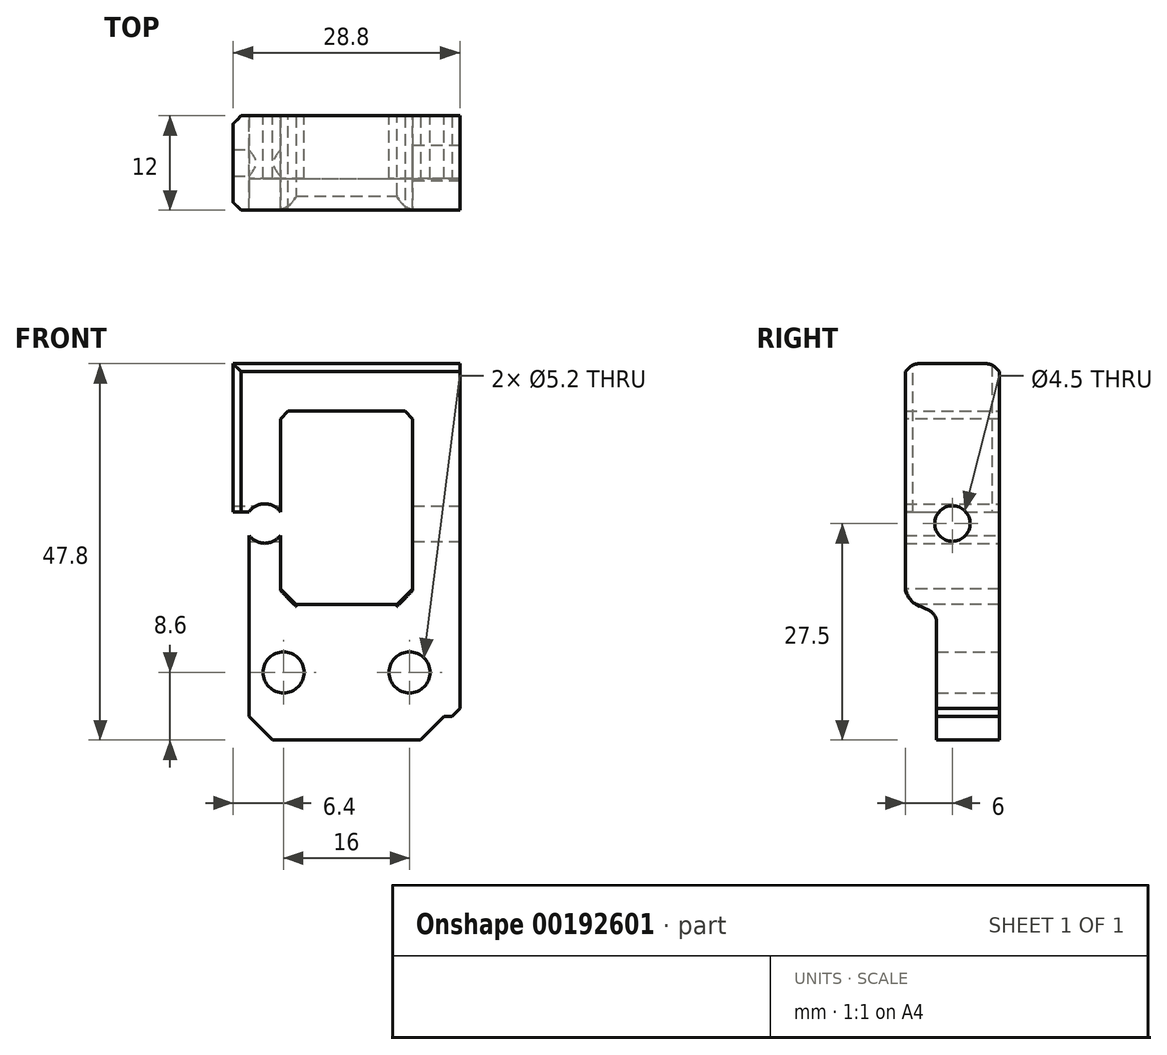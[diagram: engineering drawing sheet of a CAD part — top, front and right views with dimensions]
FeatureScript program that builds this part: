
annotation { "Feature Type Name" : "Feature", "Feature Type Description" : "" }
export const myFeature = defineFeature(function(context is Context, id is Id, definition is map)
    precondition{}
    {
        {
            var Q0;
            Q0=qCreatedBy(makeId("Front.planeOp"),FACE);
            var sketch = newSketch(context, id + "F0", { "sketchPlane" : qUnion([Q0])});
            skLineSegment(sketch, "E0", {"start": v(0, 0) * mm, "end": v(24.8, 0) * mm});
            skLineSegment(sketch, "E1", {"start": v(24.8, 0) * mm, "end": v(24.8, 41.8) * mm});
            skLineSegment(sketch, "E2", {"start": v(24.8, 41.8) * mm, "end": v(20.8, 41.8) * mm});
            skLineSegment(sketch, "E3", {"start": v(20.8, 41.8) * mm, "end": v(20.8, 17.2) * mm});
            skLineSegment(sketch, "E4", {"start": v(20.8, 17.2) * mm, "end": v(4, 17.2) * mm});
            skLineSegment(sketch, "E5", {"start": v(4, 17.2) * mm, "end": v(4, 27.5) * mm});
            skLineSegment(sketch, "E6", {"start": v(4, 27.5) * mm, "end": v(0, 27.5) * mm});
            skLineSegment(sketch, "E7", {"start": v(0, 27.5) * mm, "end": v(0, 0) * mm});
            skLineSegment(sketch, "E8", {"start": v(12.4, 17.2) * mm, "end": v(12.4, 0) * mm});
            skCircle(sketch, "E9", {"center": v(4.4, 8.6) * mm, "radius": 2.6 * mm});
            skPoint(sketch, "E9.centerSnap0", {"position": v(12.4, 8.6) * mm});
            skCircle(sketch, "E10", {"center": v(20.4, 8.6) * mm, "radius": 2.6 * mm});
            skCircle(sketch, "E11", {"center": v(2, 27.5) * mm, "radius": 2.5 * mm});
            skLineSegment(sketch, "E12.bottom", {"start": v(0, 27.5) * mm, "end": v(4, 27.5) * mm});
            skLineSegment(sketch, "E12.top", {"start": v(0, 41.8) * mm, "end": v(4, 41.8) * mm});
            skLineSegment(sketch, "E12.left", {"start": v(0, 27.5) * mm, "end": v(0, 41.8) * mm});
            skLineSegment(sketch, "E12.right", {"start": v(4, 27.5) * mm, "end": v(4, 41.8) * mm});
            skLineSegment(sketch, "E13", {"start": v(0, 41.8) * mm, "end": v(0, 47.8) * mm});
            skLineSegment(sketch, "E14", {"start": v(0, 47.8) * mm, "end": v(24.8, 47.8) * mm});
            skLineSegment(sketch, "E15", {"start": v(24.8, 47.8) * mm, "end": v(24.8, 41.8) * mm});
            skLineSegment(sketch, "E16", {"start": v(4, 41.8) * mm, "end": v(20.8, 41.8) * mm});
            skLineSegment(sketch, "E17", {"start": v(20.4, 8.6) * mm, "end": v(20.4, 11.2) * mm});
            skSolve(sketch);
        }
        {
            var Q0;
            {var subQ5=sQuery(id+"F0.wireOp",EDGE,"E12.top");Q0=makeQuery(id+"F0.imprint","IMPRINT",FACE,{"disambiguationData":[TD([[makeQuery(id+"F0.imprint","IMPRINT",EDGE,{"derivedFrom":subQ5}),-1.0]])]});}
            var Q1;
            {var subQ5=sQuery(id+"F0.wireOp",EDGE,"E12.bottom");Q1=makeQuery(id+"F0.imprint","IMPRINT",FACE,{"disambiguationData":[TD([[makeQuery(id+"F0.imprint","IMPRINT",EDGE,{"derivedFrom":subQ5}),1.0]])]});}
            var Q2;
            {var subQ0=sQuery(id+"F0.wireOp",EDGE,"E12.bottom");Q2=makeQuery(id+"F0.imprint","IMPRINT",FACE,{"disambiguationData":[TD([[makeQuery(id+"F0.imprint","IMPRINT",EDGE,{"derivedFrom":subQ0}),-1.0]])]});}
            var Q3;
            {var subQ9=sQuery(id+"F0.wireOp",EDGE,"E8");Q3=makeQuery(id+"F0.imprint","IMPRINT",FACE,{"disambiguationData":[TD([[makeQuery(id+"F0.imprint","IMPRINT",EDGE,{"derivedFrom":subQ9}),-1.0]])]});}
            var Q4;
            {var subQ1=sQuery(id+"F0.wireOp",EDGE,"E1");Q4=makeQuery(id+"F0.imprint","IMPRINT",FACE,{"disambiguationData":[TD([[makeQuery(id+"F0.imprint","IMPRINT",EDGE,{"derivedFrom":subQ1}),1.0]])]});}
            var Q5;
            Q5=makeQuery(id+"F0.imprint","IMPRINT",FACE,{"disambiguationData":[TD([[makeQuery(id+"F0.imprint","IMPRINT",EDGE,{"derivedFrom":sQuery(id+"F0.wireOp",EDGE,"E2")}),-1.0]])]});
            extrude(context, id + "F1", {"entities" : qUnion([Q0, Q1, Q2, Q3, Q4, Q5]), "depth" : 12 * mm});
        }
        {
            var Q0;
            Q0=makeQuery(id+"F1.opExtrude","SWEPT_FACE",FACE,{"disambiguationData":[OSD([sQuery(id+"F0.wireOp",EDGE,"E1")])]});
            var sketch = newSketch(context, id + "F2", { "sketchPlane" : qUnion([Q0])});
            skCircle(sketch, "E18", {"center": v(-6, 27.5) * mm, "radius": 2.25 * mm});
            skPoint(sketch, "E18.centerSnap0", {"position": v(-6, 0) * mm});
            skLineSegment(sketch, "E19", {"start": v(-8, 0) * mm, "end": v(-8, 16) * mm});
            skLineSegment(sketch, "E20", {"start": v(-8, 16) * mm, "end": v(-12, 17.87) * mm});
            skSolve(sketch);
        }
        {
            var Q0;
            {var subQ0=sQuery(id+"F2.wireOp",EDGE,"E19");Q0=makeQuery(id+"F2.imprint","IMPRINT",FACE,{"disambiguationData":[TD([[makeQuery(id+"F2.imprint","IMPRINT",EDGE,{"derivedFrom":subQ0}),1.0]])]});}
            var Q1;
            Q1=makeQuery(id+"F2.imprint","IMPRINT",FACE,{"disambiguationData":[TD([[makeQuery(id+"F2.imprint","IMPRINT",EDGE,{"derivedFrom":sQuery(id+"F2.wireOp",EDGE,"E18")}),1.0]])]});
            extrude(context, id + "F3", {"entities" : qUnion([Q0, Q1]), "operationType" : NewBodyOperationType.REMOVE, "oppositeDirection" : true, "depth" : 28.8 * mm});
        }
        {
            var Q0;
            Q0=makeQuery(id+"F1.opExtrude","SWEPT_EDGE",EDGE,{"disambiguationData":[OSD([sQuery(id+"F0.wireOp",EDGE,"E4"),sQuery(id+"F0.wireOp",EDGE,"E5")])]});
            var Q1;
            Q1=makeQuery(id+"F1.opExtrude","SWEPT_EDGE",EDGE,{"disambiguationData":[OSD([sQuery(id+"F0.wireOp",EDGE,"E3"),sQuery(id+"F0.wireOp",EDGE,"E4")])]});
            chamfer(context, id + "F4", {"entities" : qUnion([Q0, Q1]), "width" : 2 * mm, "tangentPropagation" : true});
        }
        {
            var Q0;
            Q0=makeQuery(id+"F1.opExtrude","CAP_EDGE",EDGE,{"disambiguationData":[OSD([sQuery(id+"F0.wireOp",EDGE,"E14")])],"isStart":false});
            var Q1;
            Q1=makeQuery(id+"F1.opExtrude","SWEPT_EDGE",EDGE,{"disambiguationData":[OSD([sQuery(id+"F0.wireOp",EDGE,"E12.top"),sQuery(id+"F0.wireOp",EDGE,"E12.right"),sQuery(id+"F0.wireOp",EDGE,"E16")])]});
            var Q2;
            Q2=makeQuery(id+"F1.opExtrude","SWEPT_EDGE",EDGE,{"disambiguationData":[OSD([sQuery(id+"F0.wireOp",EDGE,"E2"),sQuery(id+"F0.wireOp",EDGE,"E3"),sQuery(id+"F0.wireOp",EDGE,"E16")])]});
            var Q3;
            Q3=makeQuery(id+"F1.opExtrude","CAP_EDGE",EDGE,{"disambiguationData":[OSD([sQuery(id+"F0.wireOp",EDGE,"E14")])],"isStart":true});
            chamfer(context, id + "F5", {"entities" : qUnion([Q0, Q1, Q2, Q3]), "width" : 1 * mm, "tangentPropagation" : true});
        }
        {
            var Q0;
            {var subQ0=sQuery(id+"F0.wireOp",EDGE,"E12.right");var subQ3=sQuery(id+"F0.wireOp",EDGE,"E5");var subQ4=sQuery(id+"F0.wireOp",EDGE,"E1");var subQ5=sQuery(id+"F2.wireOp",EDGE,"E20");Q0=makeQuery(id+"F3.boolean.opBoolean","COPY",EDGE,{"disambiguationData":[TD([makeQuery(id+"F1.opExtrude","SWEPT_FACE",FACE,{"disambiguationData":[OSD([subQ3,subQ0])]})])],"derivedFrom":makeQuery(id+"F3.opExtrude","SWEPT_EDGE",EDGE,{"disambiguationData":[OSD([subQ4,subQ5])]})});}
            var Q1;
            {var subQ1=sQuery(id+"F0.wireOp",EDGE,"E1");var subQ2=sQuery(id+"F2.wireOp",EDGE,"E20");Q1=makeQuery(id+"F3.boolean.opBoolean","COPY",EDGE,{"disambiguationData":[TD([makeQuery(id+"F1.opExtrude","SWEPT_FACE",FACE,{"disambiguationData":[OSD([subQ1])]})])],"derivedFrom":makeQuery(id+"F3.opExtrude","SWEPT_EDGE",EDGE,{"disambiguationData":[OSD([subQ1,subQ2])]})});}
            fillet(context, id + "F6", {"entities" : qUnion([Q0, Q1]), "radius" : 2.7 * mm, "tangentPropagation" : true, "allowEdgeOverflow" : false});
        }
        {
            var Q0;
            Q0=makeQuery(id+"F1.opExtrude","SWEPT_EDGE",EDGE,{"disambiguationData":[OSD([sQuery(id+"F0.wireOp",EDGE,"E0"),sQuery(id+"F0.wireOp",EDGE,"E1")])]});
            var Q1;
            Q1=makeQuery(id+"F1.opExtrude","SWEPT_EDGE",EDGE,{"disambiguationData":[OSD([sQuery(id+"F0.wireOp",EDGE,"E0"),sQuery(id+"F0.wireOp",EDGE,"E7")])]});
            chamfer(context, id + "F7", {"entities" : qUnion([Q0, Q1]), "width" : 3 * mm, "tangentPropagation" : true});
        }
        {
            var Q0;
            Q0=makeQuery(id+"F1.opExtrude","SWEPT_FACE",FACE,{"disambiguationData":[OSD([sQuery(id+"F0.wireOp",EDGE,"E7"),sQuery(id+"F0.wireOp",EDGE,"E12.left"),sQuery(id+"F0.wireOp",EDGE,"E13")])]});
            extrude(context, id + "F8", {"entities" : qUnion([Q0]), "operationType" : NewBodyOperationType.ADD, "depth" : 2 * mm});
        }
        {
            var Q0;
            Q0=makeQuery(id+"F1.opExtrude","SWEPT_FACE",FACE,{"disambiguationData":[OSD([sQuery(id+"F0.wireOp",EDGE,"E1"),sQuery(id+"F0.wireOp",EDGE,"E15")])]});
            extrude(context, id + "F9", {"entities" : qUnion([Q0]), "operationType" : NewBodyOperationType.ADD, "depth" : 2 * mm});
        }
        {
            var Q0;
            Q0=makeQuery(id+"F8.opExtrude","CAP_EDGE",EDGE,{"disambiguationData":[OSD([sQuery(id+"F0.wireOp",EDGE,"E0"),sQuery(id+"F0.wireOp",EDGE,"E7"),sQuery(id+"F0.wireOp",EDGE,"E12.left"),sQuery(id+"F0.wireOp",EDGE,"E13")])],"isStart":false});
            var Q1;
            Q1=makeQuery(id+"F9.opExtrude","CAP_EDGE",EDGE,{"disambiguationData":[OSD([sQuery(id+"F0.wireOp",EDGE,"E0"),sQuery(id+"F0.wireOp",EDGE,"E1"),sQuery(id+"F0.wireOp",EDGE,"E15")])],"isStart":false});
            chamfer(context, id + "F10", {"entities" : qUnion([Q0, Q1]), "width" : 1 * mm, "tangentPropagation" : true});
        }
        {
            var Q0;
            {var subQ0=sQuery(id+"F2.wireOp",EDGE,"E20");var subQ1=sQuery(id+"F2.wireOp",EDGE,"E19");Q0=makeQuery(id+"F9.boolean.opBoolean","MERGE",EDGE,{"derivedFrom":[makeQuery(id+"F8.boolean.opBoolean","MERGE",EDGE,{"derivedFrom":[makeQuery(id+"F3.boolean.opBoolean","COPY",EDGE,{"derivedFrom":makeQuery(id+"F3.opExtrude","SWEPT_EDGE",EDGE,{"disambiguationData":[OSD([subQ1,subQ0])]})}),makeQuery(id+"F8.opExtrude","SWEPT_EDGE",EDGE,{"disambiguationData":[OSD([sQuery(id+"F0.wireOp",EDGE,"E7"),sQuery(id+"F0.wireOp",EDGE,"E12.left"),sQuery(id+"F0.wireOp",EDGE,"E13"),subQ1,subQ0])]})]}),makeQuery(id+"F9.opExtrude","SWEPT_EDGE",EDGE,{"disambiguationData":[OSD([subQ1,subQ0])]})]});}
            fillet(context, id + "F11", {"entities" : qUnion([Q0]), "radius" : 1.62 * mm, "tangentPropagation" : true, "allowEdgeOverflow" : false});
        }
        {
            var Q0;
            {var subQ0=sQuery(id+"F0.wireOp",EDGE,"E4");var subQ1=sQuery(id+"F0.wireOp",EDGE,"E15");var subQ3=sQuery(id+"F0.wireOp",EDGE,"E12.right");var subQ6=sQuery(id+"F0.wireOp",EDGE,"E5");var subQ7=sQuery(id+"F0.wireOp",EDGE,"E1");var subQ8=sQuery(id+"F2.wireOp",EDGE,"E20");Q0=makeQuery(id+"F6.opFillet","BLEND_EDGE",EDGE,{"blendedFrom":[makeQuery(id+"F3.boolean.opBoolean","COPY",EDGE,{"disambiguationData":[TD([makeQuery(id+"F1.opExtrude","SWEPT_FACE",FACE,{"disambiguationData":[OSD([subQ6,subQ3])]})])],"derivedFrom":makeQuery(id+"F3.opExtrude","SWEPT_EDGE",EDGE,{"disambiguationData":[OSD([subQ7,subQ1,subQ8])]})}),makeQuery(id+"F1.opExtrude","SWEPT_FACE",FACE,{"disambiguationData":[OSD([subQ0])]})],"blendedInto":[makeQuery(id+"F1.opExtrude","SWEPT_FACE",FACE,{"disambiguationData":[OSD([subQ0])]})]});}
            var Q1;
            {var subQ0=sQuery(id+"F0.wireOp",EDGE,"E5");var subQ1=sQuery(id+"F0.wireOp",EDGE,"E4");var subQ2=sQuery(id+"F0.wireOp",EDGE,"E15");var subQ4=sQuery(id+"F0.wireOp",EDGE,"E12.right");var subQ7=sQuery(id+"F0.wireOp",EDGE,"E1");var subQ8=sQuery(id+"F2.wireOp",EDGE,"E20");Q1=makeQuery(id+"F6.opFillet","BLEND_EDGE",EDGE,{"blendedFrom":[makeQuery(id+"F3.boolean.opBoolean","COPY",EDGE,{"disambiguationData":[TD([makeQuery(id+"F1.opExtrude","SWEPT_FACE",FACE,{"disambiguationData":[OSD([subQ0,subQ4])]})])],"derivedFrom":makeQuery(id+"F3.opExtrude","SWEPT_EDGE",EDGE,{"disambiguationData":[OSD([subQ7,subQ2,subQ8])]})}),makeQuery(id+"F4.opChamfer","BLEND_FACE",FACE,{"disambiguationData":[OSD([subQ1,subQ0])]})],"blendedInto":[makeQuery(id+"F4.opChamfer","BLEND_FACE",FACE,{"disambiguationData":[OSD([subQ1,subQ0])]})]});}
            var Q2;
            {var subQ0=sQuery(id+"F0.wireOp",EDGE,"E4");var subQ1=sQuery(id+"F0.wireOp",EDGE,"E3");var subQ2=sQuery(id+"F0.wireOp",EDGE,"E15");var subQ4=sQuery(id+"F0.wireOp",EDGE,"E12.right");var subQ7=sQuery(id+"F0.wireOp",EDGE,"E5");var subQ8=sQuery(id+"F0.wireOp",EDGE,"E1");var subQ9=sQuery(id+"F2.wireOp",EDGE,"E20");Q2=makeQuery(id+"F6.opFillet","BLEND_EDGE",EDGE,{"blendedFrom":[makeQuery(id+"F3.boolean.opBoolean","COPY",EDGE,{"disambiguationData":[TD([makeQuery(id+"F1.opExtrude","SWEPT_FACE",FACE,{"disambiguationData":[OSD([subQ7,subQ4])]})])],"derivedFrom":makeQuery(id+"F3.opExtrude","SWEPT_EDGE",EDGE,{"disambiguationData":[OSD([subQ8,subQ2,subQ9])]})}),makeQuery(id+"F4.opChamfer","BLEND_FACE",FACE,{"disambiguationData":[OSD([subQ1,subQ0])]})],"blendedInto":[makeQuery(id+"F4.opChamfer","BLEND_FACE",FACE,{"disambiguationData":[OSD([subQ1,subQ0])]})]});}
            fillet(context, id + "F12", {"entities" : qUnion([Q0, Q1, Q2]), "radius" : 0.1 * mm, "tangentPropagation" : true, "allowEdgeOverflow" : false});
        }
    });
